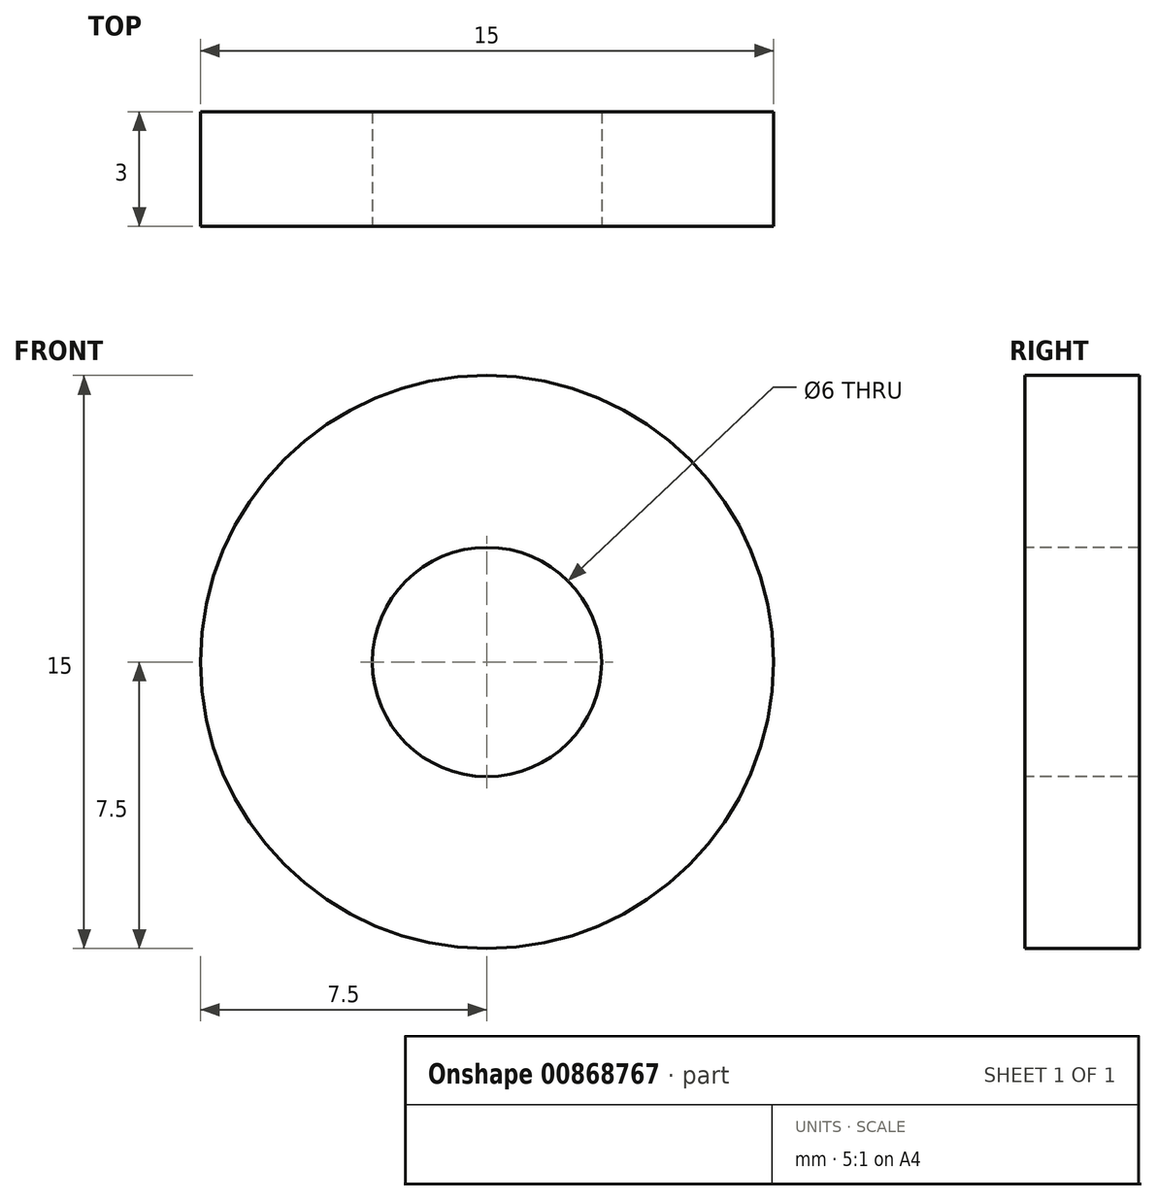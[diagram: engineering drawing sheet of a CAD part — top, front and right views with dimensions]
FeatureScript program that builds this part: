
annotation { "Feature Type Name" : "Feature", "Feature Type Description" : "" }
export const myFeature = defineFeature(function(context is Context, id is Id, definition is map)
    precondition{}
    {
        {
            var Q0;
            Q0=qCreatedBy(makeId("Front.planeOp"),FACE);
            var sketch = newSketch(context, id + "F0", { "sketchPlane" : qUnion([Q0])});
            skCircle(sketch, "E0", {"center": v(0, 0) * mm, "radius": 7.5 * mm});
            skCircle(sketch, "E1", {"center": v(0, 0) * mm, "radius": 3 * mm});
            skSolve(sketch);
        }
        {
            var Q0;
            Q0=makeQuery(id+"F0.imprint","IMPRINT",FACE,{"disambiguationData":[TD([[makeQuery(id+"F0.imprint","IMPRINT",EDGE,{"derivedFrom":sQuery(id+"F0.wireOp",EDGE,"E0")}),1.0]])]});
            extrude(context, id + "F1", {"entities" : qUnion([Q0]), "oppositeDirection" : true, "depth" : 3 * mm, "offsetDistance" : 25 * mm});
        }
    });
